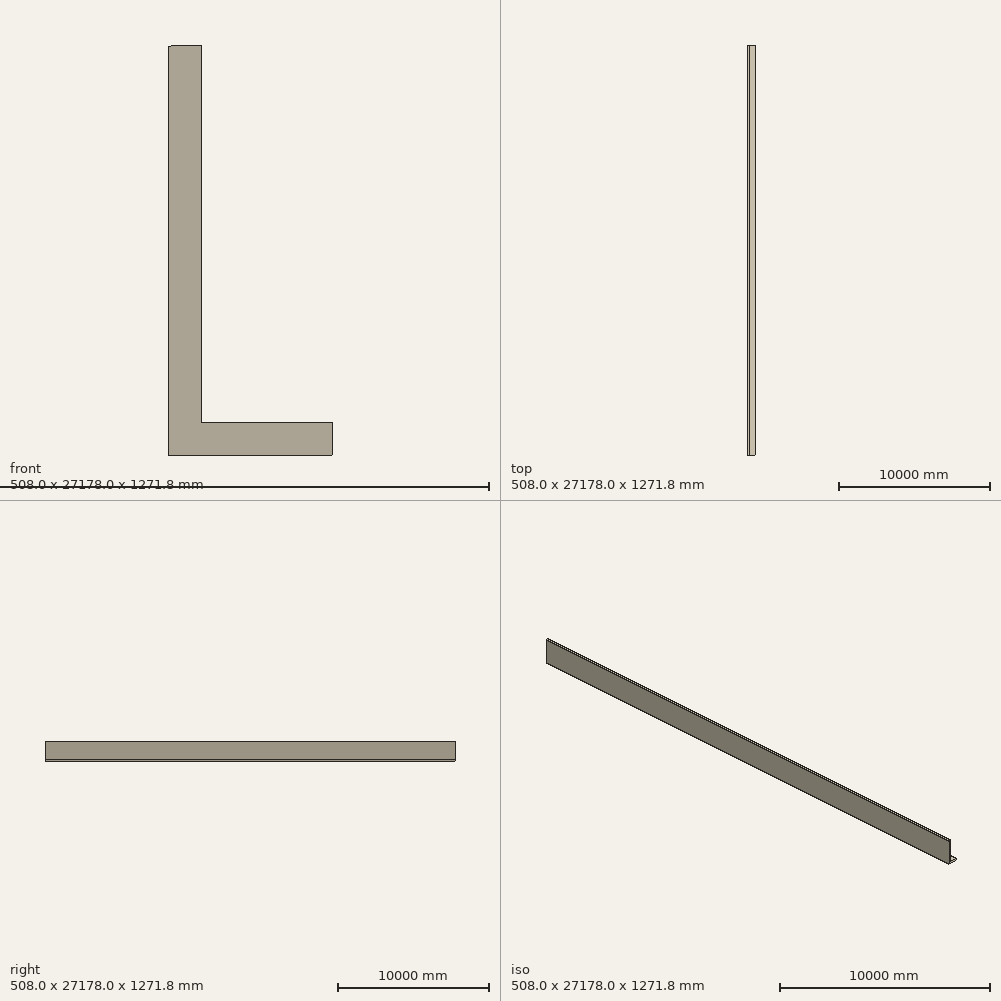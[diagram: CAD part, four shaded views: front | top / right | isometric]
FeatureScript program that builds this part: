
annotation { "Feature Type Name" : "Feature", "Feature Type Description" : "" }
export const myFeature = defineFeature(function(context is Context, id is Id, definition is map)
    precondition{}
    {
        {
            var Q0;
            Q0=qCreatedBy(makeId("Front.planeOp"),FACE);
            var sketch = newSketch(context, id + "F0", { "sketchPlane" : qUnion([Q0])});
            skLineSegment(sketch, "E0", {"start": v(-961.64, 682.88) * mm, "end": v(-961.64, -587.12) * mm});
            skLineSegment(sketch, "E1", {"start": v(-961.64, -587.12) * mm, "end": v(-453.64, -587.12) * mm});
            skLineSegment(sketch, "E2", {"start": v(-453.64, -587.12) * mm, "end": v(-453.64, -485.52) * mm});
            skLineSegment(sketch, "E3", {"start": v(-453.64, -485.52) * mm, "end": v(-860.05, -485.52) * mm});
            skLineSegment(sketch, "E4", {"start": v(-860.05, -485.52) * mm, "end": v(-860.05, 684.72) * mm});
            skLineSegment(sketch, "E5", {"start": v(-860.05, 684.72) * mm, "end": v(-961.64, 682.88) * mm});
            skSolve(sketch);
        }
        {
            var Q0;
            Q0=makeQuery(id+"F0.imprint","IMPRINT",FACE,{"disambiguationData":[TD([[makeQuery(id+"F0.imprint","IMPRINT",EDGE,{"derivedFrom":sQuery(id+"F0.wireOp",EDGE,"E0")}),1.0]])]});
            extrude(context, id + "F1", {"entities" : qUnion([Q0]), "depth" : 27178 * mm});
        }
    });
